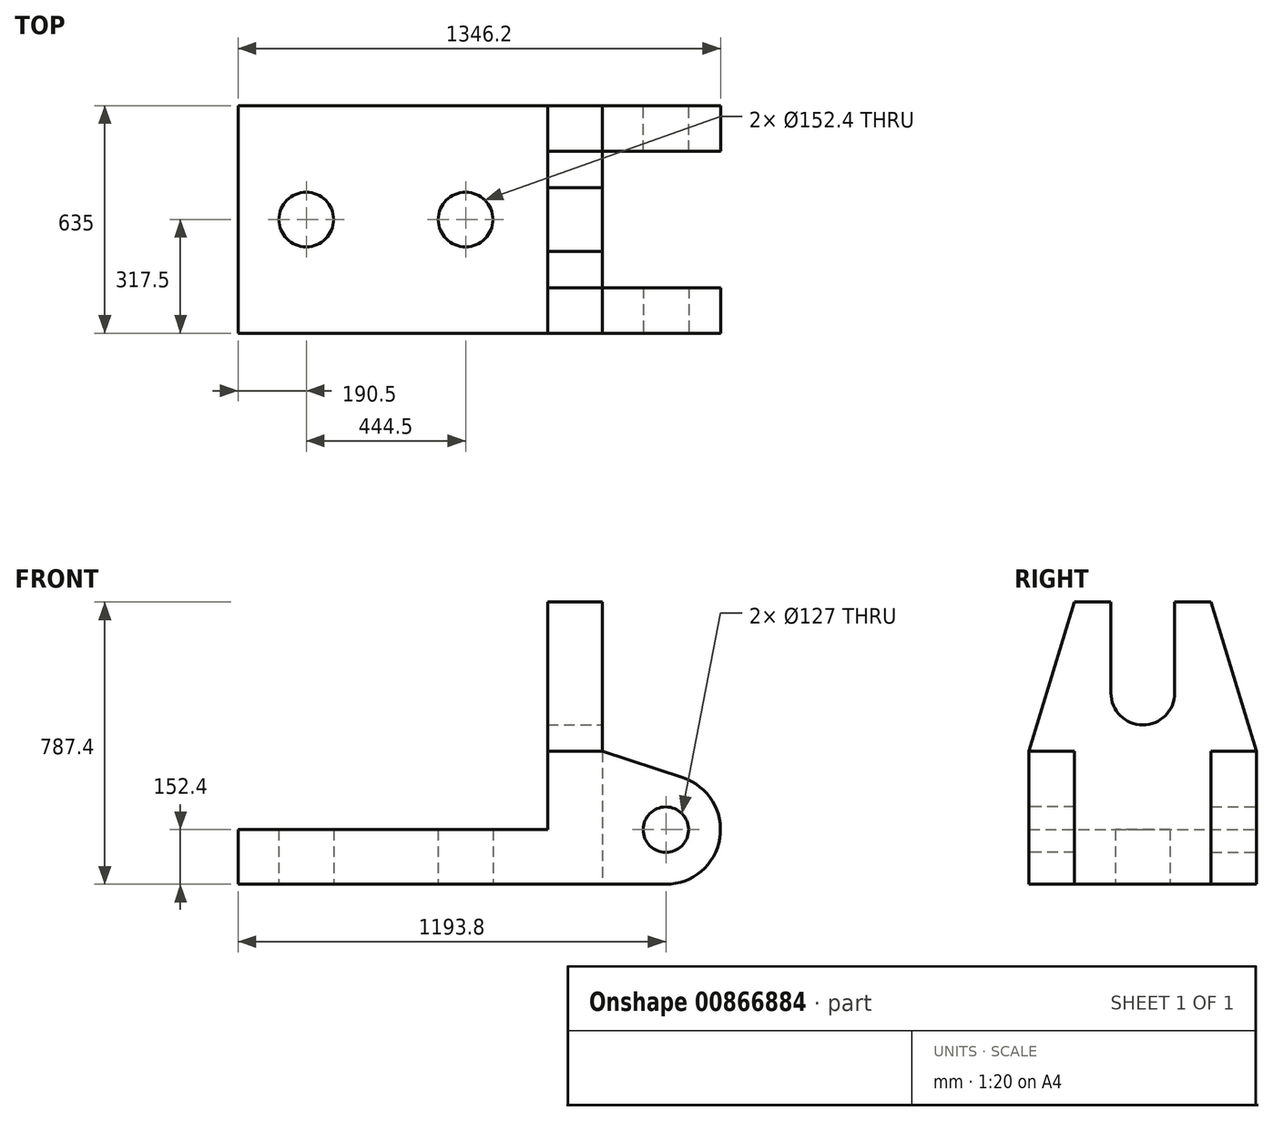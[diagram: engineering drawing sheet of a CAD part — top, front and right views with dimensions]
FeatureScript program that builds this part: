
annotation { "Feature Type Name" : "Feature", "Feature Type Description" : "" }
export const myFeature = defineFeature(function(context is Context, id is Id, definition is map)
    precondition{}
    {
        {
            var Q0;
            Q0=qCreatedBy(makeId("Top.planeOp"),FACE);
            var sketch = newSketch(context, id + "F0", { "sketchPlane" : qUnion([Q0])});
            skLineSegment(sketch, "E0.bottom", {"start": v(0, 0) * mm, "end": v(1016, 0) * mm});
            skLineSegment(sketch, "E0.top", {"start": v(0, 635) * mm, "end": v(1016, 635) * mm});
            skLineSegment(sketch, "E0.left", {"start": v(0, 0) * mm, "end": v(0, 635) * mm});
            skLineSegment(sketch, "E0.right", {"start": v(1016, 0) * mm, "end": v(1016, 635) * mm});
            skLineSegment(sketch, "E1", {"start": v(0, 317.5) * mm, "end": v(190.5, 317.5) * mm});
            skLineSegment(sketch, "E2", {"start": v(190.5, 317.5) * mm, "end": v(635, 317.5) * mm});
            skCircle(sketch, "E3", {"center": v(190.5, 317.5) * mm, "radius": 76.2 * mm});
            skCircle(sketch, "E4", {"center": v(635, 317.5) * mm, "radius": 76.2 * mm});
            skSolve(sketch);
        }
        {
            var Q0;
            {var subQ3=sQuery(id+"F0.wireOp",EDGE,"E0.bottom");Q0=makeQuery(id+"F0.imprint","IMPRINT",FACE,{"disambiguationData":[TD([[makeQuery(id+"F0.imprint","IMPRINT",EDGE,{"derivedFrom":subQ3}),1.0]])]});}
            extrude(context, id + "F1", {"entities" : qUnion([Q0]), "depth" : 152.4 * mm, "offsetDistance" : 25.4 * mm});
        }
        {
            var Q0;
            Q0=makeQuery(id+"F1.opExtrude","SWEPT_FACE",FACE,{"disambiguationData":[OSD([sQuery(id+"F0.wireOp",EDGE,"E0.right")])]});
            var sketch = newSketch(context, id + "F2", { "sketchPlane" : qUnion([Q0])});
            skLineSegment(sketch, "E5.bottom", {"start": v(0, -10.23) * mm, "end": v(635, -10.23) * mm});
            skLineSegment(sketch, "E5.top", {"start": v(0, 370.77) * mm, "end": v(635, 370.77) * mm});
            skLineSegment(sketch, "E5.left", {"start": v(0, -10.23) * mm, "end": v(0, 370.77) * mm});
            skLineSegment(sketch, "E5.right", {"start": v(635, -10.23) * mm, "end": v(635, 370.77) * mm});
            skLineSegment(sketch, "E6", {"start": v(317.5, 152.4) * mm, "end": v(317.5, 533.4) * mm});
            skArc(sketch, "E7", {"start": v(406.4, 533.4) * mm, "mid": v(317.5, 444.5) * mm, "end": v(228.6, 533.4) * mm});
            skLineSegment(sketch, "E8", {"start": v(228.6, 533.4) * mm, "end": v(228.6, 787.4) * mm});
            skLineSegment(sketch, "E9", {"start": v(228.6, 787.4) * mm, "end": v(127, 787.4) * mm});
            skLineSegment(sketch, "E10", {"start": v(127, 787.4) * mm, "end": v(0, 370.77) * mm});
            skLineSegment(sketch, "E11", {"start": v(406.4, 533.4) * mm, "end": v(406.4, 787.4) * mm});
            skLineSegment(sketch, "E12", {"start": v(406.4, 787.4) * mm, "end": v(508, 787.4) * mm});
            skLineSegment(sketch, "E13", {"start": v(508, 787.4) * mm, "end": v(635, 370.77) * mm});
            skSolve(sketch);
        }
        {
            var Q0;
            {var subQ0=sQuery(id+"F2.wireOp",EDGE,"E11");Q0=makeQuery(id+"F2.imprint","IMPRINT",FACE,{"disambiguationData":[TD([[makeQuery(id+"F2.imprint","IMPRINT",EDGE,{"derivedFrom":subQ0}),-1.0]])]});}
            var Q1;
            {var subQ3=sQuery(id+"F2.wireOp",EDGE,"E6");var subQ5=makeQuery(id+"F1.opExtrude","CAP_EDGE",EDGE,{"disambiguationData":[OSD([sQuery(id+"F0.wireOp",EDGE,"E0.right")])],"isStart":false});var subQ7=makeQuery(id+"F2.imprint","INTERSECT",VERTEX,{"derivedFrom":[subQ5,subQ3]});Q1=makeQuery(id+"F2.imprint","IMPRINT",FACE,{"disambiguationData":[TD([[makeQuery(id+"F2.imprint","IMPRINT",EDGE,{"disambiguationData":[TD([[subQ7,-1.0]])],"derivedFrom":subQ3}),-1.0]])]});}
            var Q2;
            {var subQ3=sQuery(id+"F2.wireOp",EDGE,"E6");var subQ5=makeQuery(id+"F1.opExtrude","CAP_EDGE",EDGE,{"disambiguationData":[OSD([sQuery(id+"F0.wireOp",EDGE,"E0.right")])],"isStart":false});var subQ7=makeQuery(id+"F2.imprint","INTERSECT",VERTEX,{"derivedFrom":[subQ5,subQ3]});Q2=makeQuery(id+"F2.imprint","IMPRINT",FACE,{"disambiguationData":[TD([[makeQuery(id+"F2.imprint","IMPRINT",EDGE,{"disambiguationData":[TD([[subQ7,-1.0]])],"derivedFrom":subQ3}),1.0]])]});}
            var Q3;
            {var subQ0=sQuery(id+"F2.wireOp",EDGE,"E8");Q3=makeQuery(id+"F2.imprint","IMPRINT",FACE,{"disambiguationData":[TD([[makeQuery(id+"F2.imprint","IMPRINT",EDGE,{"derivedFrom":subQ0}),1.0]])]});}
            extrude(context, id + "F3", {"entities" : qUnion([Q0, Q1, Q2, Q3]), "operationType" : NewBodyOperationType.ADD, "oppositeDirection" : true, "depth" : 152.4 * mm, "offsetDistance" : 25.4 * mm});
        }
        {
            var Q0;
            Q0=makeQuery(id+"F3.boolean.opBoolean","MERGE",FACE,{"derivedFrom":[makeQuery(id+"F1.opExtrude","SWEPT_FACE",FACE,{"disambiguationData":[OSD([sQuery(id+"F0.wireOp",EDGE,"E0.bottom")])]}),makeQuery(id+"F3.opExtrude","SWEPT_FACE",FACE,{"disambiguationData":[OSD([sQuery(id+"F2.wireOp",EDGE,"E5.left")])]})]});
            var sketch = newSketch(context, id + "F4", { "sketchPlane" : qUnion([Q0])});
            skLineSegment(sketch, "E14", {"start": v(1016, 0) * mm, "end": v(1193.8, 0) * mm});
            skArc(sketch, "E15", {"start": v(1193.8, 0) * mm, "mid": v(1346.2, 152.4) * mm, "end": v(1193.8, 304.8) * mm});
            skLineSegment(sketch, "E16", {"start": v(1016, 370.77) * mm, "end": v(1241.1, 297.27) * mm});
            skCircle(sketch, "E17", {"center": v(1193.8, 152.4) * mm, "radius": 63.5 * mm});
            skSolve(sketch);
        }
        {
            var Q0;
            {var subQ2=sQuery(id+"F4.wireOp",EDGE,"E14");Q0=makeQuery(id+"F4.imprint","IMPRINT",FACE,{"disambiguationData":[TD([[makeQuery(id+"F4.imprint","IMPRINT",EDGE,{"derivedFrom":subQ2}),1.0]])]});}
            extrude(context, id + "F5", {"entities" : qUnion([Q0]), "operationType" : NewBodyOperationType.ADD, "oppositeDirection" : true, "depth" : 127 * mm, "offsetDistance" : 25.4 * mm});
        }
        {
            var Q0;
            Q0=makeQuery(id+"F3.boolean.opBoolean","MERGE",FACE,{"derivedFrom":[makeQuery(id+"F1.opExtrude","SWEPT_FACE",FACE,{"disambiguationData":[OSD([sQuery(id+"F0.wireOp",EDGE,"E0.top")])]}),makeQuery(id+"F3.opExtrude","SWEPT_FACE",FACE,{"disambiguationData":[OSD([sQuery(id+"F2.wireOp",EDGE,"E5.right")])]})]});
            var sketch = newSketch(context, id + "F6", { "sketchPlane" : qUnion([Q0])});
            skLineSegment(sketch, "E18.0.0", {"start": v(-1016, 370.77) * mm, "end": v(-1241.1, 297.27) * mm});
            skArc(sketch, "E18.0.1", {"start": v(-1241.1, 297.27) * mm, "mid": v(-1344.3, 128.45) * mm, "end": v(-1193.8, 0) * mm});
            skLineSegment(sketch, "E18.0.2", {"start": v(-1193.8, 0) * mm, "end": v(-1016, 0) * mm});
            skLineSegment(sketch, "E18.0.3", {"start": v(-1016, 0) * mm, "end": v(-1016, 370.77) * mm});
            skCircle(sketch, "E19", {"center": v(-1193.8, 152.4) * mm, "radius": 63.5 * mm});
            skSolve(sketch);
        }
        {
            var Q0;
            Q0=makeQuery(id+"F6.imprint","IMPRINT",FACE,{"disambiguationData":[TD([[makeQuery(id+"F6.imprint","IMPRINT",EDGE,{"derivedFrom":sQuery(id+"F6.wireOp",EDGE,"E18.0.0")}),1.0]])]});
            extrude(context, id + "F7", {"entities" : qUnion([Q0]), "operationType" : NewBodyOperationType.ADD, "oppositeDirection" : true, "depth" : 127 * mm, "offsetDistance" : 25.4 * mm});
        }
    });
